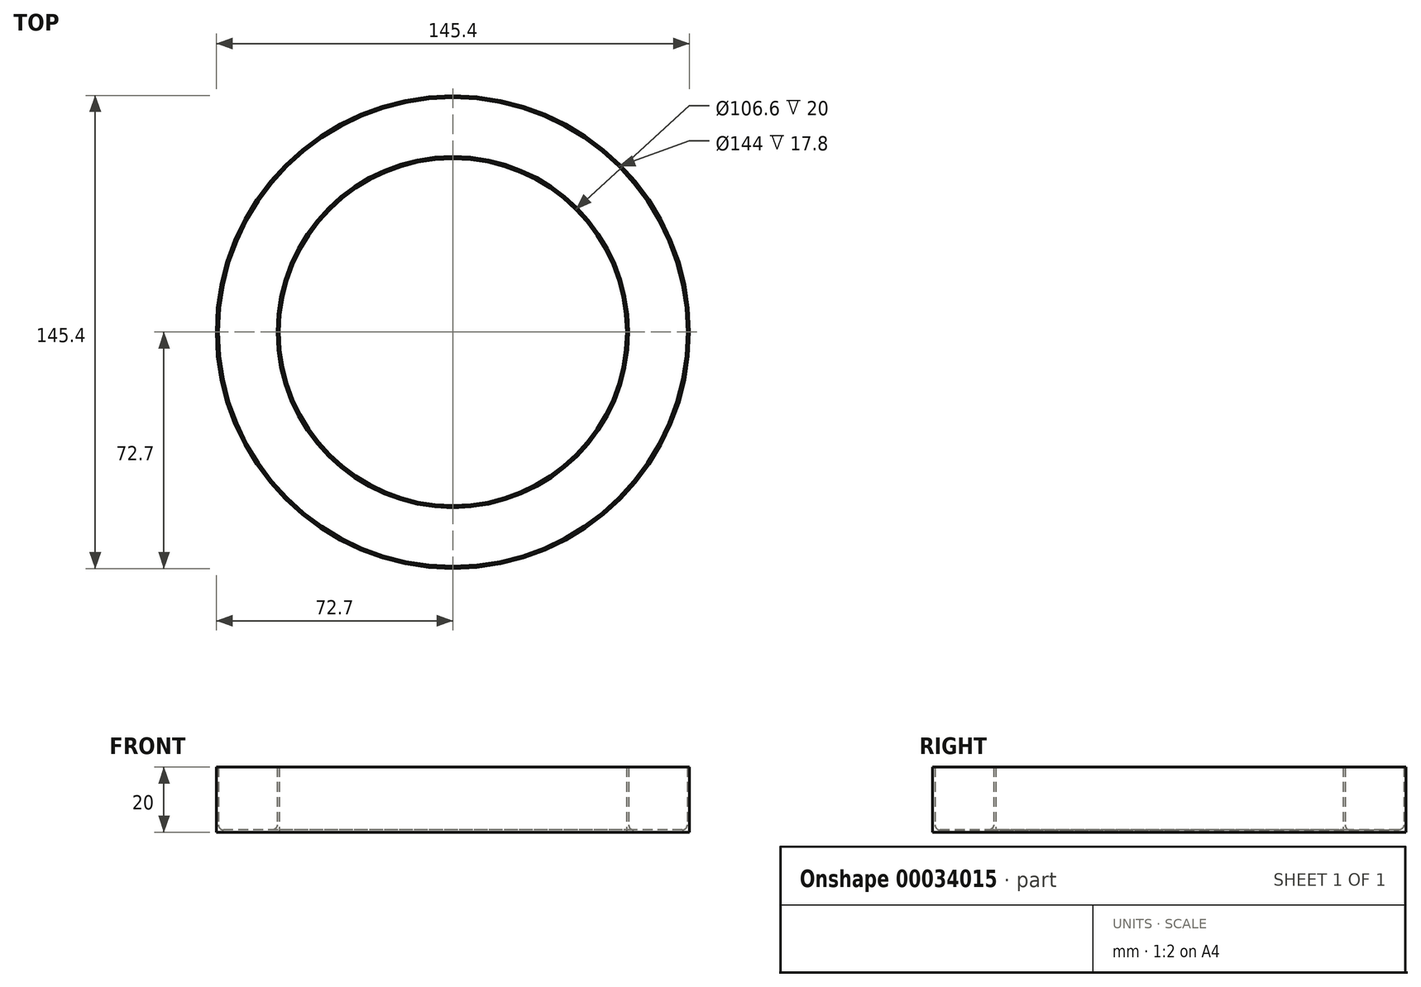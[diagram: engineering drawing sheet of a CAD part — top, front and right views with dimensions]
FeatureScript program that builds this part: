
annotation { "Feature Type Name" : "Feature", "Feature Type Description" : "" }
export const myFeature = defineFeature(function(context is Context, id is Id, definition is map)
    precondition{}
    {
        {
            var Q0;
            Q0=qCreatedBy(makeId("Top.planeOp"),FACE);
            var sketch = newSketch(context, id + "F0", { "sketchPlane" : qUnion([Q0])});
            skCircle(sketch, "E0", {"center": v(0, 0) * mm, "radius": 72.7 * mm});
            skCircle(sketch, "E1", {"center": v(0, 0) * mm, "radius": 53.3 * mm});
            skSolve(sketch);
        }
        {
            var Q0;
            Q0=makeQuery(id+"F0.imprint","IMPRINT",FACE,{"disambiguationData":[TD([[makeQuery(id+"F0.imprint","IMPRINT",EDGE,{"derivedFrom":sQuery(id+"F0.wireOp",EDGE,"E0")}),1.0]])]});
            extrude(context, id + "F1", {"entities" : qUnion([Q0]), "depth" : 20 * mm});
        }
        {
            var Q0;
            Q0=makeQuery(id+"F1.opExtrude","CAP_FACE",FACE,{"disambiguationData":[OSD([sQuery(id+"F0.wireOp",EDGE,"E0"),sQuery(id+"F0.wireOp",EDGE,"E1")])],"isStart":false});
            shell(context, id + "F2", {"entities" : qUnion([Q0]), "thickness" : 0.7 * mm});
        }
        {
            var Q0;
            {var subQ0=sQuery(id+"F0.wireOp",EDGE,"E0");Q0=makeQuery(id+"F2.opShell","OFFSET_EDGE",EDGE,{"disambiguationData":[OSD([subQ0]),TDD([makeQuery(id+"F1.opExtrude","CAP_EDGE",EDGE,{"disambiguationData":[OSD([subQ0])],"isStart":true})])]});}
            var Q1;
            {var subQ0=sQuery(id+"F0.wireOp",EDGE,"E1");Q1=makeQuery(id+"F2.opShell","OFFSET_EDGE",EDGE,{"disambiguationData":[OSD([subQ0]),TDD([makeQuery(id+"F1.opExtrude","CAP_EDGE",EDGE,{"disambiguationData":[OSD([subQ0])],"isStart":true})])]});}
            fillet(context, id + "F3", {"entities" : qUnion([Q0, Q1]), "radius" : 1.5 * mm, "tangentPropagation" : true, "allowEdgeOverflow" : false});
        }
    });
